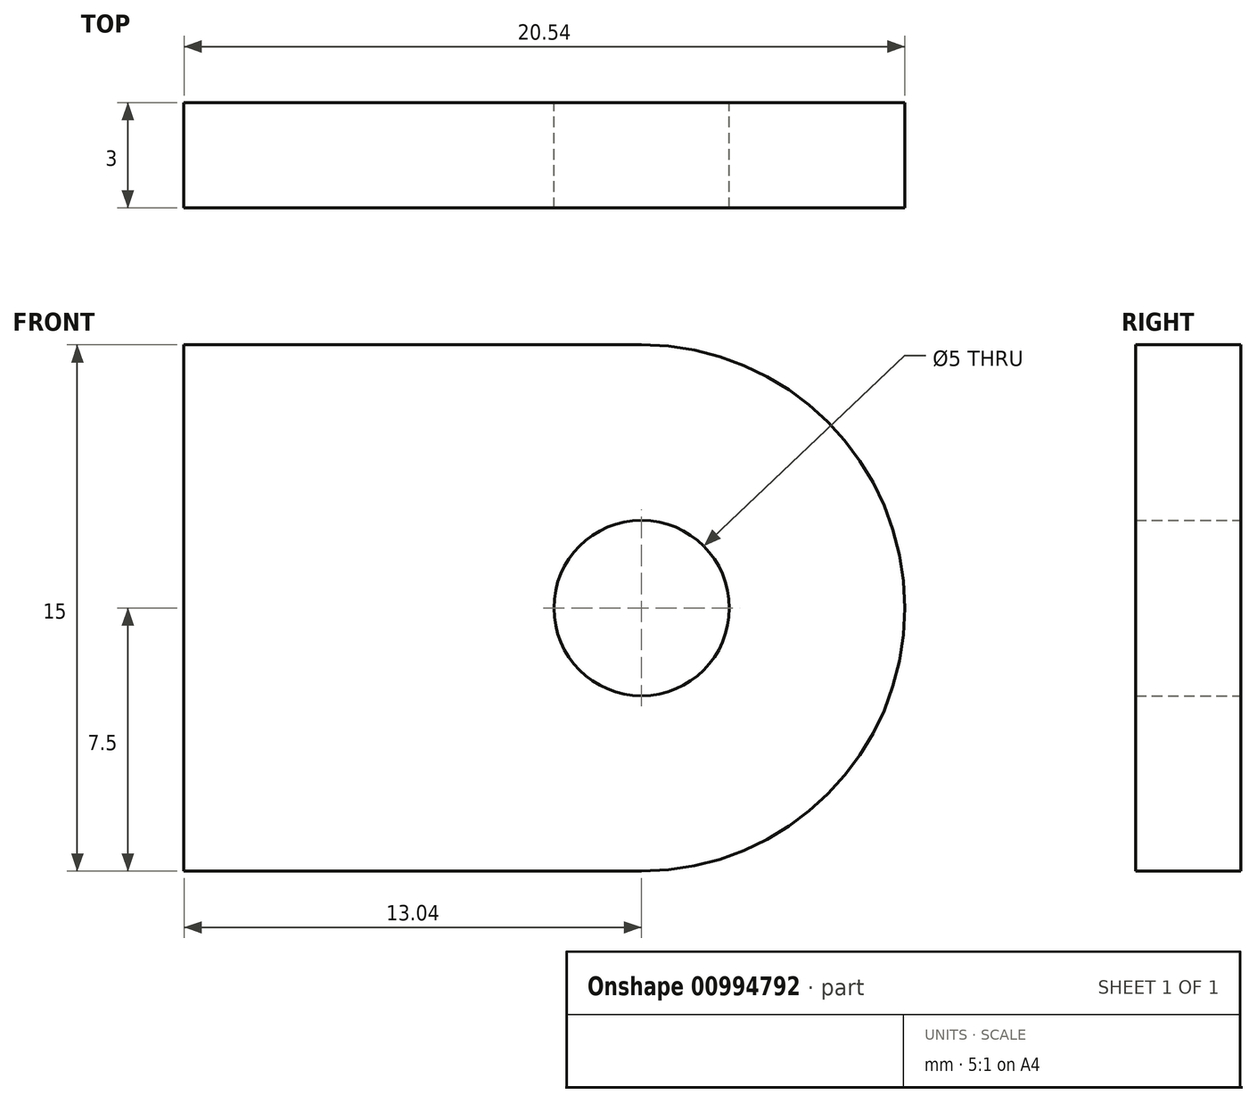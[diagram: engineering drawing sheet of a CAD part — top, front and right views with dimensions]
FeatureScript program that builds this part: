
annotation { "Feature Type Name" : "Feature", "Feature Type Description" : "" }
export const myFeature = defineFeature(function(context is Context, id is Id, definition is map)
    precondition{}
    {
        {
            var Q0;
            Q0=qCreatedBy(makeId("Front.planeOp"),FACE);
            var sketch = newSketch(context, id + "F0", { "sketchPlane" : qUnion([Q0])});
            skCircle(sketch, "E0", {"center": v(0, 0) * mm, "radius": 7.5 * mm});
            skCircle(sketch, "E1", {"center": v(0, 0) * mm, "radius": 2.5 * mm});
            skLineSegment(sketch, "E2", {"start": v(0, 0) * mm, "end": v(0, -7.5) * mm});
            skLineSegment(sketch, "E3.MirrorCS", {"start": v(0, 0) * mm, "end": v(0, 7.5) * mm});
            skLineSegment(sketch, "E4", {"start": v(-13.04, 7.5) * mm, "end": v(-13.04, -7.5) * mm});
            skLineSegment(sketch, "E5", {"start": v(-13.04, -7.5) * mm, "end": v(0, -7.5) * mm});
            skLineSegment(sketch, "E6", {"start": v(-13.04, 7.5) * mm, "end": v(0, 7.5) * mm});
            skLineSegment(sketch, "E7", {"start": v(-7.5, 0) * mm, "end": v(-7.5, -7.5) * mm});
            skLineSegment(sketch, "E8", {"start": v(-7.5, 0) * mm, "end": v(-7.5, 7.5) * mm});
            skSolve(sketch);
        }
        {
            var Q0;
            Q0 = qSketchRegion(id + "F0", true);
            extrude(context, id + "F1", {"entities" : qUnion([Q0]), "endBound" : BoundingType.SYMMETRIC, "depth" : 3 * mm, "offsetDistance" : 25.4 * mm});
        }
    });
